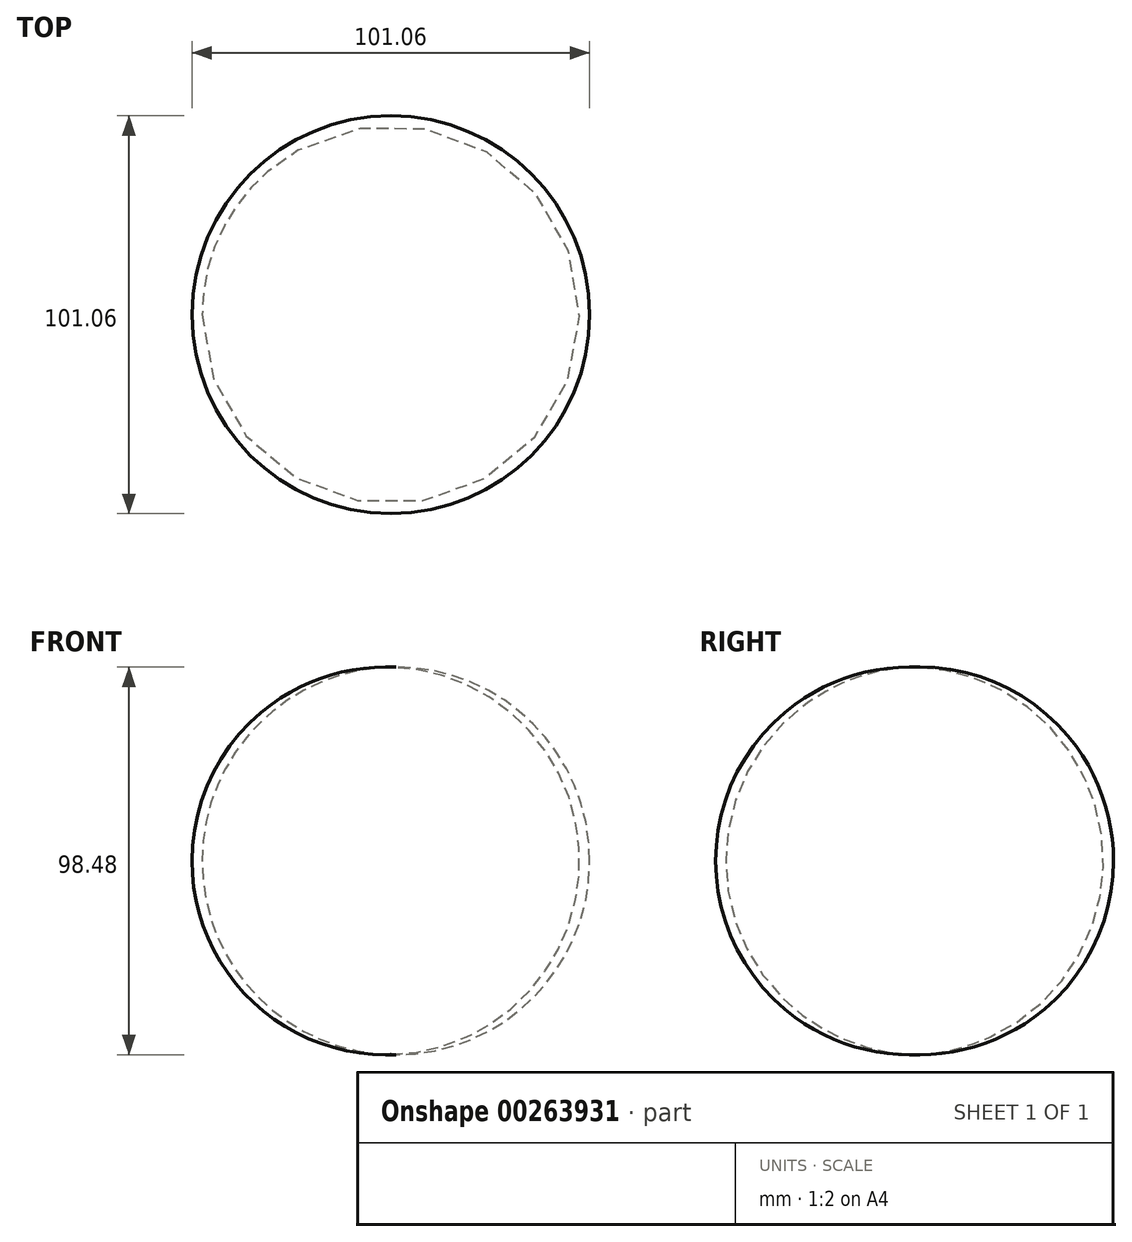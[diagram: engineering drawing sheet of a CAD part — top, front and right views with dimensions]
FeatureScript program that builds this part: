
annotation { "Feature Type Name" : "Feature", "Feature Type Description" : "" }
export const myFeature = defineFeature(function(context is Context, id is Id, definition is map)
    precondition{}
    {
        {
            var Q0;
            Q0=qCreatedBy(makeId("Front.planeOp"),FACE);
            var sketch = newSketch(context, id + "F0", { "sketchPlane" : qUnion([Q0])});
            skArc(sketch, "E0", {"start": v(0, -49.22) * mm, "mid": v(50.53, 0) * mm, "end": v(0, 49.22) * mm});
            skLineSegment(sketch, "E1", {"start": v(0, 49.22) * mm, "end": v(0, -49.22) * mm});
            skSolve(sketch);
        }
        {
            var Q0;
            Q0=makeQuery(id+"F0.imprint","IMPRINT",FACE,{"disambiguationData":[TD([[makeQuery(id+"F0.imprint","IMPRINT",EDGE,{"derivedFrom":sQuery(id+"F0.wireOp",EDGE,"E0")}),1.0]])]});
            var Q1;
            Q1=sQuery(id+"F0.wireOp",EDGE,"E1");
            revolve(context, id + "F1", {"entities" : qUnion([Q0]), "axis" : qUnion([Q1]), "revolveType" : RevolveType.FULL});
        }
    });
